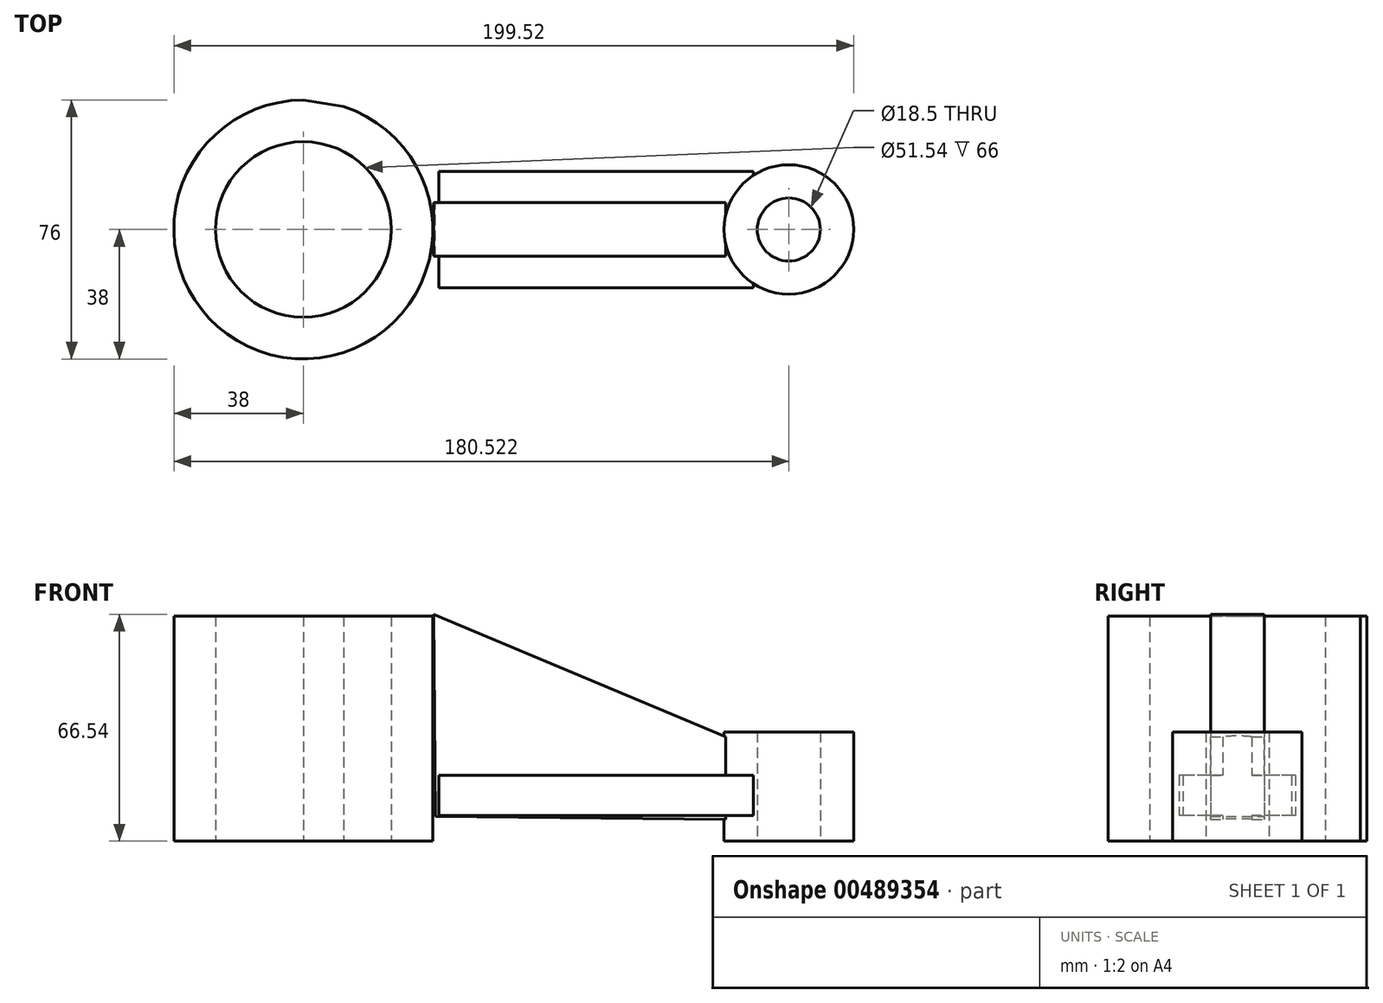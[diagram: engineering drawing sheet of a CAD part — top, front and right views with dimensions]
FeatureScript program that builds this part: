
annotation { "Feature Type Name" : "Feature", "Feature Type Description" : "" }
export const myFeature = defineFeature(function(context is Context, id is Id, definition is map)
    precondition{}
    {
        {
            var Q0;
            Q0=qCreatedBy(makeId("Top.planeOp"),FACE);
            var sketch = newSketch(context, id + "F0", { "sketchPlane" : qUnion([Q0])});
            skCircle(sketch, "E0", {"center": v(0, 0) * mm, "radius": 38 * mm});
            skLineSegment(sketch, "E1", {"start": v(0, 38) * mm, "end": v(133.5, 16.72) * mm});
            skLineSegment(sketch, "E2", {"start": v(5.32, -37.63) * mm, "end": v(139.17, -18.7) * mm});
            skCircle(sketch, "E3", {"center": v(142.52, 0) * mm, "radius": 19 * mm});
            skCircle(sketch, "E4", {"center": v(0, 0) * mm, "radius": 25.77 * mm});
            skLineSegment(sketch, "E5", {"start": v(37.26, 7.48) * mm, "end": v(125.05, 7.48) * mm});
            skLineSegment(sketch, "E6", {"start": v(124.38, -5.65) * mm, "end": v(37.58, -5.65) * mm});
            skCircle(sketch, "E7", {"center": v(142.52, 0) * mm, "radius": 9.25 * mm});
            skSolve(sketch);
        }
        {
            var Q0;
            Q0=sQuery(id+"F0.wireOp",EDGE,"E7");
            extrude(context, id + "F1", {"bodyType" : ToolBodyType.SURFACE, "surfaceEntities" : qUnion([Q0]), "depth" : 21 * mm, "offsetDistance" : 25 * mm});
        }
        {
            var Q0;
            Q0=makeQuery(id+"F0.imprint","IMPRINT",FACE,{"disambiguationData":[TD([[makeQuery(id+"F0.imprint","IMPRINT",EDGE,{"derivedFrom":sQuery(id+"F0.wireOp",EDGE,"E7")}),-1.0]])]});
            var Q1;
            Q1=sQuery(id+"F0.wireOp",EDGE,"E3");
            extrude(context, id + "F2", {"entities" : qUnion([Q0]), "surfaceEntities" : qUnion([Q1]), "depth" : 32 * mm, "offsetDistance" : 25 * mm});
        }
        {
            var Q0;
            Q0=makeQuery(id+"F0.imprint","IMPRINT",FACE,{"disambiguationData":[TD([[makeQuery(id+"F0.imprint","IMPRINT",EDGE,{"derivedFrom":sQuery(id+"F0.wireOp",EDGE,"E4")}),-1.0]])]});
            extrude(context, id + "F3", {"entities" : qUnion([Q0]), "depth" : 66 * mm, "offsetDistance" : 25 * mm});
        }
        {
            var Q0;
            Q0=qCreatedBy(makeId("Front.planeOp"),FACE);
            var sketch = newSketch(context, id + "F4", { "sketchPlane" : qUnion([Q0])});
            skLineSegment(sketch, "E8", {"start": v(38.21, 66.54) * mm, "end": v(124, 30.64) * mm});
            skLineSegment(sketch, "E9", {"start": v(38.78, 7.27) * mm, "end": v(124, 6.41) * mm});
            skLineSegment(sketch, "E10", {"start": v(38.21, 66.54) * mm, "end": v(38.78, 7.27) * mm});
            skLineSegment(sketch, "E11", {"start": v(124, 6.41) * mm, "end": v(124, 30.64) * mm});
            skSolve(sketch);
        }
        {
            var Q0;
            Q0=makeQuery(id+"F4.imprint","IMPRINT",FACE,{"disambiguationData":[TD([[makeQuery(id+"F4.imprint","IMPRINT",EDGE,{"derivedFrom":sQuery(id+"F4.wireOp",EDGE,"E8")}),-1.0]])]});
            extrude(context, id + "F5", {"entities" : qUnion([Q0]), "operationType" : NewBodyOperationType.ADD, "endBound" : BoundingType.SYMMETRIC, "depth" : 15.8 * mm, "offsetDistance" : 25 * mm});
        }
        {
            var Q0;
            Q0=qCreatedBy(makeId("Front.planeOp"),FACE);
            var sketch = newSketch(context, id + "F6", { "sketchPlane" : qUnion([Q0])});
            skLineSegment(sketch, "E12.bottom", {"start": v(132.16, 19.26) * mm, "end": v(39.72, 19.26) * mm});
            skLineSegment(sketch, "E12.top", {"start": v(132.16, 7.5) * mm, "end": v(39.72, 7.5) * mm});
            skLineSegment(sketch, "E12.left", {"start": v(132.16, 19.26) * mm, "end": v(132.16, 7.5) * mm});
            skLineSegment(sketch, "E12.right", {"start": v(-52.71, 19.26) * mm, "end": v(-52.71, 7.5) * mm});
            skPoint(sketch, "E12.middle", {"position": v(39.72, 13.38) * mm});
            skLineSegment(sketch, "E13", {"start": v(39.72, 19.26) * mm, "end": v(39.72, 7.5) * mm});
            skSolve(sketch);
        }
        {
            var Q0;
            Q0 = qSketchRegion(id + "F6", true);
            extrude(context, id + "F7", {"entities" : qUnion([Q0]), "operationType" : NewBodyOperationType.ADD, "endBound" : BoundingType.SYMMETRIC, "oppositeDirection" : true, "depth" : 34.2 * mm, "offsetDistance" : 25 * mm});
        }
    });
